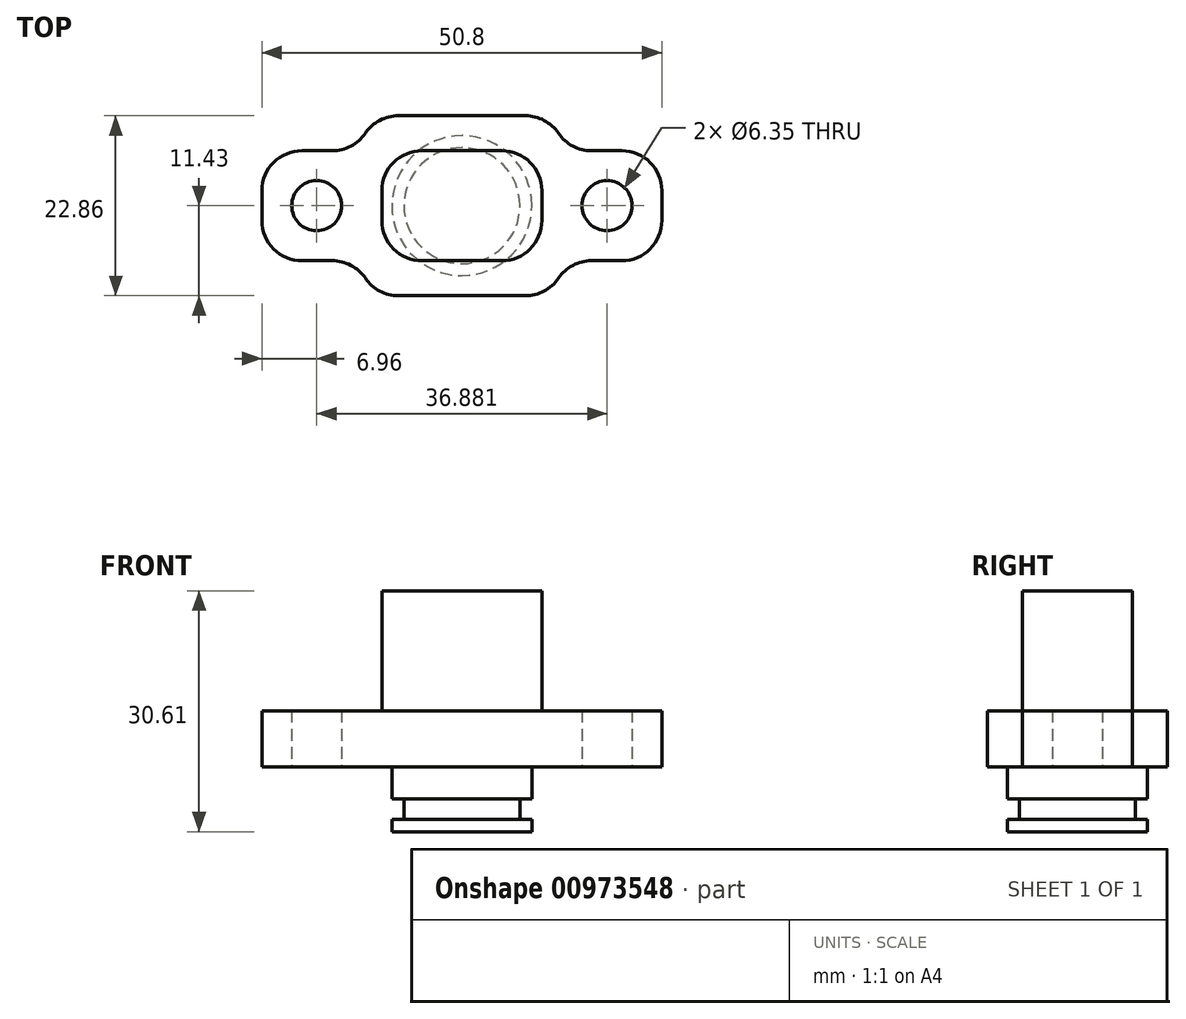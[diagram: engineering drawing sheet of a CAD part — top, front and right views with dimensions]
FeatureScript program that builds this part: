
annotation { "Feature Type Name" : "Feature", "Feature Type Description" : "" }
export const myFeature = defineFeature(function(context is Context, id is Id, definition is map)
    precondition{}
    {
        {
            var Q0;
            Q0=qCreatedBy(makeId("Top.planeOp"),FACE);
            var sketch = newSketch(context, id + "F0", { "sketchPlane" : qUnion([Q0])});
            skCircle(sketch, "E0", {"center": v(0, 0) * mm, "radius": 8.9 * mm});
            skLineSegment(sketch, "E1.bottom", {"start": v(25.4, 6.99) * mm, "end": v(-25.4, 6.99) * mm});
            skLineSegment(sketch, "E1.top", {"start": v(25.4, -6.99) * mm, "end": v(-25.4, -6.99) * mm});
            skLineSegment(sketch, "E1.left", {"start": v(25.4, 6.99) * mm, "end": v(25.4, -6.99) * mm});
            skLineSegment(sketch, "E1.right", {"start": v(-25.4, 6.99) * mm, "end": v(-25.4, -6.99) * mm});
            skCircle(sketch, "E2", {"center": v(-18.44, 0) * mm, "radius": 3.18 * mm});
            skCircle(sketch, "E3", {"center": v(18.44, 0) * mm, "radius": 3.18 * mm});
            skLineSegment(sketch, "E4.bottom", {"start": v(10.16, 9.53) * mm, "end": v(-10.16, 9.52) * mm});
            skLineSegment(sketch, "E4.top", {"start": v(10.16, -9.52) * mm, "end": v(-10.16, -9.53) * mm});
            skLineSegment(sketch, "E4.left", {"start": v(10.16, 9.53) * mm, "end": v(10.16, -9.52) * mm});
            skLineSegment(sketch, "E4.right", {"start": v(-10.16, 9.52) * mm, "end": v(-10.16, -9.53) * mm});
            skCircle(sketch, "E5", {"center": v(0, 0) * mm, "radius": 7.37 * mm});
            skLineSegment(sketch, "E6.bottom", {"start": v(11.43, 11.43) * mm, "end": v(-11.43, 11.43) * mm});
            skLineSegment(sketch, "E6.top", {"start": v(11.43, -11.43) * mm, "end": v(-11.43, -11.43) * mm});
            skLineSegment(sketch, "E6.left", {"start": v(11.43, 11.43) * mm, "end": v(11.43, -11.43) * mm});
            skLineSegment(sketch, "E6.right", {"start": v(-11.43, 11.43) * mm, "end": v(-11.43, -11.43) * mm});
            skSolve(sketch);
        }
        {
            var Q0;
            Q0=makeQuery(id+"F0.imprint","IMPRINT",FACE,{"disambiguationData":[TD([[makeQuery(id+"F0.imprint","IMPRINT",EDGE,{"derivedFrom":sQuery(id+"F0.wireOp",EDGE,"E0")}),1.0]])]});
            var Q1;
            Q1=makeQuery(id+"F0.imprint","IMPRINT",FACE,{"disambiguationData":[TD([[makeQuery(id+"F0.imprint","IMPRINT",EDGE,{"derivedFrom":sQuery(id+"F0.wireOp",EDGE,"E5")}),1.0]])]});
            var Q2;
            {var subQ0=sQuery(id+"F0.wireOp",EDGE,"E5");var subQ1=sQuery(id+"F0.wireOp",EDGE,"E1.bottom");var subQ2=makeQuery(id+"F0.imprint","INTERSECT",VERTEX,{"disambiguationData":[OD(0.0)],"derivedFrom":[subQ1,subQ0]});Q2=makeQuery(id+"F0.imprint","IMPRINT",FACE,{"disambiguationData":[TD([[makeQuery(id+"F0.imprint","IMPRINT",EDGE,{"disambiguationData":[TD([[subQ2,-1.0]])],"derivedFrom":subQ1}),-1.0]])]});}
            var Q3;
            {var subQ0=sQuery(id+"F0.wireOp",EDGE,"E5");var subQ1=sQuery(id+"F0.wireOp",EDGE,"E1.top");var subQ2=makeQuery(id+"F0.imprint","INTERSECT",VERTEX,{"disambiguationData":[OD(0.0)],"derivedFrom":[subQ1,subQ0]});Q3=makeQuery(id+"F0.imprint","IMPRINT",FACE,{"disambiguationData":[TD([[makeQuery(id+"F0.imprint","IMPRINT",EDGE,{"disambiguationData":[TD([[subQ2,-1.0]])],"derivedFrom":subQ1}),1.0]])]});}
            var Q4;
            Q4=sQuery(id+"F0.wireOp",EDGE,"E0");
            extrude(context, id + "F1", {"entities" : qUnion([Q0, Q1, Q2, Q3]), "surfaceEntities" : qUnion([Q4]), "oppositeDirection" : true, "depth" : 8.25 * mm, "offsetDistance" : 25.4 * mm});
        }
        {
            var Q0;
            Q0=makeQuery(id+"F0.imprint","IMPRINT",FACE,{"disambiguationData":[TD([[makeQuery(id+"F0.imprint","IMPRINT",EDGE,{"derivedFrom":sQuery(id+"F0.wireOp",EDGE,"E1.bottom")}),1.0]])]});
            var Q1;
            Q1=makeQuery(id+"F0.imprint","IMPRINT",FACE,{"disambiguationData":[TD([[makeQuery(id+"F0.imprint","IMPRINT",EDGE,{"derivedFrom":sQuery(id+"F0.wireOp",EDGE,"E0")}),-1.0]])]});
            var Q2;
            Q2=makeQuery(id+"F0.imprint","IMPRINT",FACE,{"disambiguationData":[TD([[makeQuery(id+"F0.imprint","IMPRINT",EDGE,{"derivedFrom":sQuery(id+"F0.wireOp",EDGE,"E0")}),1.0]])]});
            var Q3;
            {var subQ1=sQuery(id+"F0.wireOp",EDGE,"E4.bottom");Q3=makeQuery(id+"F0.imprint","IMPRINT",FACE,{"disambiguationData":[TD([[makeQuery(id+"F0.imprint","IMPRINT",EDGE,{"derivedFrom":subQ1}),-1.0]])]});}
            var Q4;
            {var subQ0=sQuery(id+"F0.wireOp",EDGE,"E4.bottom");Q4=makeQuery(id+"F0.imprint","IMPRINT",FACE,{"disambiguationData":[TD([[makeQuery(id+"F0.imprint","IMPRINT",EDGE,{"derivedFrom":subQ0}),1.0]])]});}
            var Q5;
            {var subQ0=sQuery(id+"F0.wireOp",EDGE,"E5");var subQ1=sQuery(id+"F0.wireOp",EDGE,"E1.bottom");var subQ2=makeQuery(id+"F0.imprint","INTERSECT",VERTEX,{"disambiguationData":[OD(0.0)],"derivedFrom":[subQ1,subQ0]});Q5=makeQuery(id+"F0.imprint","IMPRINT",FACE,{"disambiguationData":[TD([[makeQuery(id+"F0.imprint","IMPRINT",EDGE,{"disambiguationData":[TD([[subQ2,-1.0]])],"derivedFrom":subQ1}),-1.0]])]});}
            var Q6;
            {var subQ0=sQuery(id+"F0.wireOp",EDGE,"E5");var subQ1=sQuery(id+"F0.wireOp",EDGE,"E1.top");var subQ2=makeQuery(id+"F0.imprint","INTERSECT",VERTEX,{"disambiguationData":[OD(0.0)],"derivedFrom":[subQ1,subQ0]});Q6=makeQuery(id+"F0.imprint","IMPRINT",FACE,{"disambiguationData":[TD([[makeQuery(id+"F0.imprint","IMPRINT",EDGE,{"disambiguationData":[TD([[subQ2,-1.0]])],"derivedFrom":subQ1}),1.0]])]});}
            var Q7;
            {var subQ6=sQuery(id+"F0.wireOp",EDGE,"E4.top");Q7=makeQuery(id+"F0.imprint","IMPRINT",FACE,{"disambiguationData":[TD([[makeQuery(id+"F0.imprint","IMPRINT",EDGE,{"derivedFrom":subQ6}),-1.0]])]});}
            var Q8;
            {var subQ0=sQuery(id+"F0.wireOp",EDGE,"E4.top");Q8=makeQuery(id+"F0.imprint","IMPRINT",FACE,{"disambiguationData":[TD([[makeQuery(id+"F0.imprint","IMPRINT",EDGE,{"derivedFrom":subQ0}),1.0]])]});}
            var Q9;
            {var subQ0=sQuery(id+"F0.wireOp",EDGE,"E1.left");Q9=makeQuery(id+"F0.imprint","IMPRINT",FACE,{"disambiguationData":[TD([[makeQuery(id+"F0.imprint","IMPRINT",EDGE,{"derivedFrom":subQ0}),-1.0]])]});}
            var Q10;
            {var subQ0=sQuery(id+"F0.wireOp",EDGE,"E1.right");Q10=makeQuery(id+"F0.imprint","IMPRINT",FACE,{"disambiguationData":[TD([[makeQuery(id+"F0.imprint","IMPRINT",EDGE,{"derivedFrom":subQ0}),1.0]])]});}
            extrude(context, id + "F2", {"entities" : qUnion([Q0, Q1, Q2, Q3, Q4, Q5, Q6, Q7, Q8, Q9, Q10]), "operationType" : NewBodyOperationType.ADD, "depth" : 7.11 * mm, "offsetDistance" : 25.4 * mm});
        }
        {
            var Q0;
            Q0=makeQuery(id+"F0.imprint","IMPRINT",FACE,{"disambiguationData":[TD([[makeQuery(id+"F0.imprint","IMPRINT",EDGE,{"derivedFrom":sQuery(id+"F0.wireOp",EDGE,"E0")}),-1.0]])]});
            var Q1;
            Q1=makeQuery(id+"F0.imprint","IMPRINT",FACE,{"disambiguationData":[TD([[makeQuery(id+"F0.imprint","IMPRINT",EDGE,{"derivedFrom":sQuery(id+"F0.wireOp",EDGE,"E5")}),1.0]])]});
            var Q2;
            {var subQ0=sQuery(id+"F0.wireOp",EDGE,"E1.bottom");var subQ1=sQuery(id+"F0.wireOp",EDGE,"E0");var subQ2=makeQuery(id+"F0.imprint","INTERSECT",VERTEX,{"disambiguationData":[OD(0.0)],"derivedFrom":[subQ1,subQ0]});Q2=makeQuery(id+"F0.imprint","IMPRINT",FACE,{"disambiguationData":[TD([[makeQuery(id+"F0.imprint","IMPRINT",EDGE,{"disambiguationData":[TD([[subQ2,-1.0]])],"derivedFrom":subQ1}),1.0]])]});}
            var Q3;
            {var subQ0=sQuery(id+"F0.wireOp",EDGE,"E1.bottom");var subQ1=sQuery(id+"F0.wireOp",EDGE,"E0");var subQ2=makeQuery(id+"F0.imprint","INTERSECT",VERTEX,{"disambiguationData":[OD(1.0)],"derivedFrom":[subQ1,subQ0]});Q3=makeQuery(id+"F0.imprint","IMPRINT",FACE,{"disambiguationData":[TD([[makeQuery(id+"F0.imprint","IMPRINT",EDGE,{"disambiguationData":[TD([[subQ2,1.0]])],"derivedFrom":subQ1}),1.0]])]});}
            extrude(context, id + "F3", {"entities" : qUnion([Q0, Q1, Q2, Q3]), "operationType" : NewBodyOperationType.ADD, "depth" : 22.35 * mm, "offsetDistance" : 25.4 * mm});
        }
        {
            var Q0;
            Q0=makeQuery(id+"F0.imprint","IMPRINT",FACE,{"disambiguationData":[TD([[makeQuery(id+"F0.imprint","IMPRINT",EDGE,{"derivedFrom":sQuery(id+"F0.wireOp",EDGE,"E0")}),1.0]])]});
            extrude(context, id + "F4", {"entities" : qUnion([Q0]), "operationType" : NewBodyOperationType.REMOVE, "oppositeDirection" : true, "depth" : 6.68 * mm, "offsetDistance" : 25.4 * mm, "hasSecondDirection" : true, "secondDirectionOppositeDirection" : true, "secondDirectionDepth" : 4.06 * mm});
        }
        {
            var Q0;
            Q0=makeQuery(id+"F2.opExtrude","SWEPT_EDGE",EDGE,{"disambiguationData":[OSD([sQuery(id+"F0.wireOp",EDGE,"E1.bottom"),sQuery(id+"F0.wireOp",EDGE,"E1.left")])]});
            var Q1;
            Q1=makeQuery(id+"F2.opExtrude","SWEPT_EDGE",EDGE,{"disambiguationData":[OSD([sQuery(id+"F0.wireOp",EDGE,"E1.top"),sQuery(id+"F0.wireOp",EDGE,"E1.left")])]});
            var Q2;
            Q2=makeQuery(id+"F2.opExtrude","SWEPT_EDGE",EDGE,{"disambiguationData":[OSD([sQuery(id+"F0.wireOp",EDGE,"E1.top"),sQuery(id+"F0.wireOp",EDGE,"E6.left")])]});
            var Q3;
            Q3=makeQuery(id+"F2.opExtrude","SWEPT_EDGE",EDGE,{"disambiguationData":[OSD([sQuery(id+"F0.wireOp",EDGE,"E1.bottom"),sQuery(id+"F0.wireOp",EDGE,"E6.left")])]});
            var Q4;
            Q4=makeQuery(id+"F2.opExtrude","SWEPT_EDGE",EDGE,{"disambiguationData":[OSD([sQuery(id+"F0.wireOp",EDGE,"E1.top"),sQuery(id+"F0.wireOp",EDGE,"E6.right")])]});
            var Q5;
            Q5=makeQuery(id+"F2.opExtrude","SWEPT_EDGE",EDGE,{"disambiguationData":[OSD([sQuery(id+"F0.wireOp",EDGE,"E1.top"),sQuery(id+"F0.wireOp",EDGE,"E1.right")])]});
            var Q6;
            Q6=makeQuery(id+"F2.opExtrude","SWEPT_EDGE",EDGE,{"disambiguationData":[OSD([sQuery(id+"F0.wireOp",EDGE,"E1.bottom"),sQuery(id+"F0.wireOp",EDGE,"E1.right")])]});
            var Q7;
            Q7=makeQuery(id+"F2.opExtrude","SWEPT_EDGE",EDGE,{"disambiguationData":[OSD([sQuery(id+"F0.wireOp",EDGE,"E1.bottom"),sQuery(id+"F0.wireOp",EDGE,"E6.right")])]});
            fillet(context, id + "F5", {"entities" : qUnion([Q0, Q1, Q2, Q3, Q4, Q5, Q6, Q7]), "radius" : 5.08 * mm, "tangentPropagation" : true, "allowEdgeOverflow" : false});
        }
        {
            var Q0;
            Q0=makeQuery(id+"F5.opFillet","BLEND_EDGE",EDGE,{"blendedFrom":[makeQuery(id+"F2.opExtrude","SWEPT_EDGE",EDGE,{"disambiguationData":[OSD([sQuery(id+"F0.wireOp",EDGE,"E1.top"),sQuery(id+"F0.wireOp",EDGE,"E6.left")])]}),makeQuery(id+"F2.opExtrude","SWEPT_FACE",FACE,{"disambiguationData":[OSD([sQuery(id+"F0.wireOp",EDGE,"E6.top")])]})],"blendedInto":[makeQuery(id+"F2.opExtrude","SWEPT_FACE",FACE,{"disambiguationData":[OSD([sQuery(id+"F0.wireOp",EDGE,"E6.top")])]})]});
            var Q1;
            Q1=makeQuery(id+"F5.opFillet","BLEND_EDGE",EDGE,{"blendedFrom":[makeQuery(id+"F2.opExtrude","SWEPT_EDGE",EDGE,{"disambiguationData":[OSD([sQuery(id+"F0.wireOp",EDGE,"E1.bottom"),sQuery(id+"F0.wireOp",EDGE,"E6.left")])]}),makeQuery(id+"F2.opExtrude","SWEPT_FACE",FACE,{"disambiguationData":[OSD([sQuery(id+"F0.wireOp",EDGE,"E6.bottom")])]})],"blendedInto":[makeQuery(id+"F2.opExtrude","SWEPT_FACE",FACE,{"disambiguationData":[OSD([sQuery(id+"F0.wireOp",EDGE,"E6.bottom")])]})]});
            var Q2;
            Q2=makeQuery(id+"F5.opFillet","BLEND_EDGE",EDGE,{"blendedFrom":[makeQuery(id+"F2.opExtrude","SWEPT_EDGE",EDGE,{"disambiguationData":[OSD([sQuery(id+"F0.wireOp",EDGE,"E1.bottom"),sQuery(id+"F0.wireOp",EDGE,"E6.right")])]}),makeQuery(id+"F2.opExtrude","SWEPT_FACE",FACE,{"disambiguationData":[OSD([sQuery(id+"F0.wireOp",EDGE,"E6.bottom")])]})],"blendedInto":[makeQuery(id+"F2.opExtrude","SWEPT_FACE",FACE,{"disambiguationData":[OSD([sQuery(id+"F0.wireOp",EDGE,"E6.bottom")])]})]});
            var Q3;
            Q3=makeQuery(id+"F5.opFillet","BLEND_EDGE",EDGE,{"blendedFrom":[makeQuery(id+"F2.opExtrude","SWEPT_EDGE",EDGE,{"disambiguationData":[OSD([sQuery(id+"F0.wireOp",EDGE,"E1.top"),sQuery(id+"F0.wireOp",EDGE,"E6.right")])]}),makeQuery(id+"F2.opExtrude","SWEPT_FACE",FACE,{"disambiguationData":[OSD([sQuery(id+"F0.wireOp",EDGE,"E6.top")])]})],"blendedInto":[makeQuery(id+"F2.opExtrude","SWEPT_FACE",FACE,{"disambiguationData":[OSD([sQuery(id+"F0.wireOp",EDGE,"E6.top")])]})]});
            fillet(context, id + "F6", {"entities" : qUnion([Q0, Q1, Q2, Q3]), "radius" : 5.08 * mm, "tangentPropagation" : true, "allowEdgeOverflow" : false});
        }
        {
            var Q0;
            Q0=makeQuery(id+"F3.opExtrude","SWEPT_EDGE",EDGE,{"disambiguationData":[OSD([sQuery(id+"F0.wireOp",EDGE,"E1.bottom"),sQuery(id+"F0.wireOp",EDGE,"E4.right")])]});
            var Q1;
            Q1=makeQuery(id+"F3.opExtrude","SWEPT_EDGE",EDGE,{"disambiguationData":[OSD([sQuery(id+"F0.wireOp",EDGE,"E1.bottom"),sQuery(id+"F0.wireOp",EDGE,"E4.left")])]});
            var Q2;
            Q2=makeQuery(id+"F3.opExtrude","SWEPT_EDGE",EDGE,{"disambiguationData":[OSD([sQuery(id+"F0.wireOp",EDGE,"E1.top"),sQuery(id+"F0.wireOp",EDGE,"E4.left")])]});
            var Q3;
            Q3=makeQuery(id+"F3.opExtrude","SWEPT_EDGE",EDGE,{"disambiguationData":[OSD([sQuery(id+"F0.wireOp",EDGE,"E1.top"),sQuery(id+"F0.wireOp",EDGE,"E4.right")])]});
            fillet(context, id + "F7", {"entities" : qUnion([Q0, Q1, Q2, Q3]), "radius" : 5.08 * mm, "tangentPropagation" : true, "allowEdgeOverflow" : false});
        }
    });
